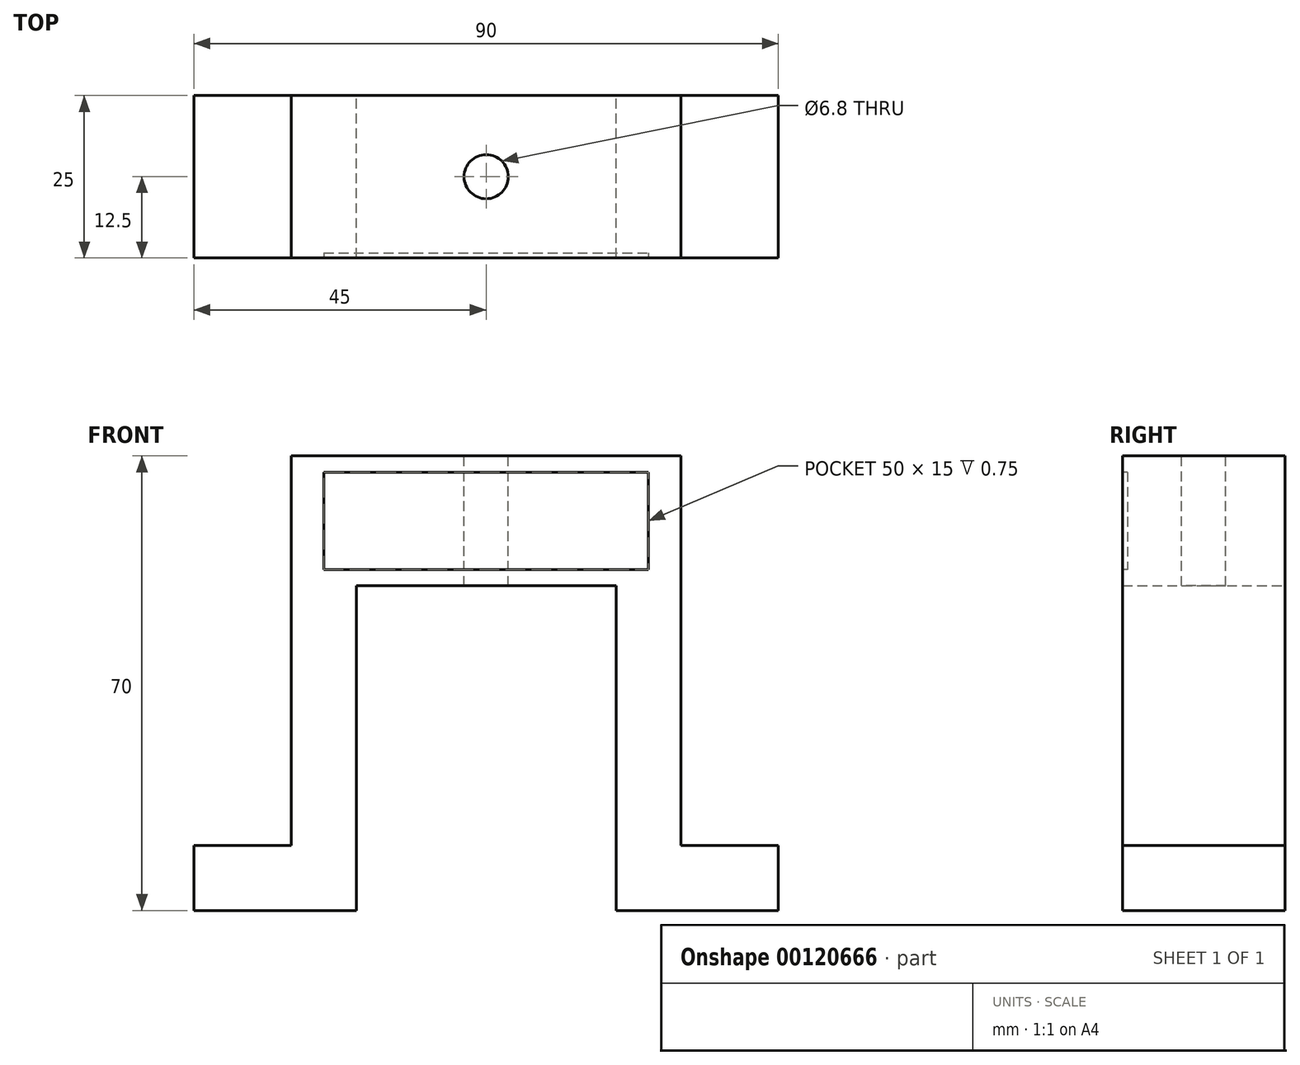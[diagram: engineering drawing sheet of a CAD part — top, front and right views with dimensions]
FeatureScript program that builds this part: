
annotation { "Feature Type Name" : "Feature", "Feature Type Description" : "" }
export const myFeature = defineFeature(function(context is Context, id is Id, definition is map)
    precondition{}
    {
        {
            var Q0;
            Q0=qCreatedBy(makeId("Front.planeOp"),FACE);
            var sketch = newSketch(context, id + "F0", { "sketchPlane" : qUnion([Q0])});
            skLineSegment(sketch, "E0", {"start": v(0, 60) * mm, "end": v(30, 60) * mm});
            skLineSegment(sketch, "E1", {"start": v(30, 60) * mm, "end": v(30, 10) * mm});
            skLineSegment(sketch, "E2", {"start": v(30, 10) * mm, "end": v(45, 10) * mm});
            skLineSegment(sketch, "E3", {"start": v(45, 10) * mm, "end": v(45, 0) * mm});
            skLineSegment(sketch, "E4", {"start": v(45, 0) * mm, "end": v(20, 0) * mm});
            skLineSegment(sketch, "E5", {"start": v(20, 0) * mm, "end": v(20, 50) * mm});
            skLineSegment(sketch, "E6", {"start": v(20, 50) * mm, "end": v(0, 50) * mm});
            skLineSegment(sketch, "E7.MirrorCS", {"start": v(0, 60) * mm, "end": v(-30, 60) * mm});
            skLineSegment(sketch, "E8.MirrorCS", {"start": v(-20, 50) * mm, "end": v(0, 50) * mm});
            skLineSegment(sketch, "E9.MirrorCS", {"start": v(-20, 0) * mm, "end": v(-20, 50) * mm});
            skLineSegment(sketch, "E10.MirrorCS", {"start": v(-30, 60) * mm, "end": v(-30, 10) * mm});
            skLineSegment(sketch, "E11.MirrorCS", {"start": v(-30, 10) * mm, "end": v(-45, 10) * mm});
            skLineSegment(sketch, "E12.MirrorCS", {"start": v(-45, 0) * mm, "end": v(-20, 0) * mm});
            skLineSegment(sketch, "E13.MirrorCS", {"start": v(-45, 10) * mm, "end": v(-45, 0) * mm});
            skSolve(sketch);
        }
        {
            var Q0;
            Q0=makeQuery(id+"F0.imprint","IMPRINT",FACE,{"disambiguationData":[TD([[makeQuery(id+"F0.imprint","IMPRINT",EDGE,{"derivedFrom":sQuery(id+"F0.wireOp",EDGE,"E0")}),-1.0]])]});
            extrude(context, id + "F1", {"entities" : qUnion([Q0]), "depth" : 25 * mm});
        }
        {
            var Q0;
            Q0=makeQuery(id+"F1.opExtrude","SWEPT_FACE",FACE,{"disambiguationData":[OSD([sQuery(id+"F0.wireOp",EDGE,"E0"),sQuery(id+"F0.wireOp",EDGE,"E7.MirrorCS")])]});
            var sketch = newSketch(context, id + "F2", { "sketchPlane" : qUnion([Q0])});
            skPoint(sketch, "E14.0", {"position": v(-30, 0) * mm});
            skPoint(sketch, "E15.0", {"position": v(30, -25) * mm});
            skLineSegment(sketch, "E16", {"start": v(-30, 0) * mm, "end": v(30, -25) * mm, "construction": true});
            skPoint(sketch, "E17", {"position": v(0, -12.5) * mm});
            skSolve(sketch);
        }
        {
            var Q0;
            Q0=sQuery(id+"F2.wireOp",VERTEX,"E17");
            var Q1;
            Q1=makeQuery(id+"F1.opExtrude","SWEPT_BODY",BODY,{"disambiguationData":[OSD([sQuery(id+"F0.wireOp",EDGE,"E0"),sQuery(id+"F0.wireOp",EDGE,"E1"),sQuery(id+"F0.wireOp",EDGE,"E2"),sQuery(id+"F0.wireOp",EDGE,"E3"),sQuery(id+"F0.wireOp",EDGE,"E4"),sQuery(id+"F0.wireOp",EDGE,"E5"),sQuery(id+"F0.wireOp",EDGE,"E6"),sQuery(id+"F0.wireOp",EDGE,"E7.MirrorCS"),sQuery(id+"F0.wireOp",EDGE,"E8.MirrorCS"),sQuery(id+"F0.wireOp",EDGE,"E9.MirrorCS"),sQuery(id+"F0.wireOp",EDGE,"E10.MirrorCS"),sQuery(id+"F0.wireOp",EDGE,"E11.MirrorCS"),sQuery(id+"F0.wireOp",EDGE,"E12.MirrorCS"),sQuery(id+"F0.wireOp",EDGE,"E13.MirrorCS")])]});
            hole(context, id + "F3", {"style" : HoleStyle.SIMPLE, "endStyle" : HoleEndStyle.BLIND, "standardTappedOrClearance" : lookupTablePath({ "standard" : "ISO", "engagement" : "75%", "pitch" : "1.25 mm", "size" : "M8", "type" : "Tapped" }), "standardBlindInLast" : lookupTablePath({ "standard" : "ISO", "engagement" : "75%", "pitch" : "1.25 mm", "size" : "M8", "type" : "Tapped" }), "holeDiameter" : 6.8 * mm, "holeDepth" : 14 * mm, "startFromSketch" : true, "locations" : qUnion([Q0]), "scope" : qUnion([Q1]), "majorDiameter" : 8 * mm});
        }
        {
            var Q0;
            Q0=makeQuery(id+"F1.opExtrude","SWEPT_FACE",FACE,{"disambiguationData":[OSD([sQuery(id+"F0.wireOp",EDGE,"E0"),sQuery(id+"F0.wireOp",EDGE,"E7.MirrorCS")])]});
            extrude(context, id + "F4", {"entities" : qUnion([Q0]), "operationType" : NewBodyOperationType.ADD, "depth" : 10 * mm});
        }
        {
            var Q0;
            {var subQ0=sQuery(id+"F0.wireOp",EDGE,"E7.MirrorCS");var subQ1=sQuery(id+"F0.wireOp",EDGE,"E0");Q0=makeQuery(id+"F4.boolean.opBoolean","MERGE",FACE,{"derivedFrom":[makeQuery(id+"F1.opExtrude","CAP_FACE",FACE,{"disambiguationData":[OSD([subQ1,sQuery(id+"F0.wireOp",EDGE,"E1"),sQuery(id+"F0.wireOp",EDGE,"E2"),sQuery(id+"F0.wireOp",EDGE,"E3"),sQuery(id+"F0.wireOp",EDGE,"E4"),sQuery(id+"F0.wireOp",EDGE,"E5"),sQuery(id+"F0.wireOp",EDGE,"E6"),subQ0,sQuery(id+"F0.wireOp",EDGE,"E8.MirrorCS"),sQuery(id+"F0.wireOp",EDGE,"E9.MirrorCS"),sQuery(id+"F0.wireOp",EDGE,"E10.MirrorCS"),sQuery(id+"F0.wireOp",EDGE,"E11.MirrorCS"),sQuery(id+"F0.wireOp",EDGE,"E12.MirrorCS"),sQuery(id+"F0.wireOp",EDGE,"E13.MirrorCS")])],"isStart":false}),makeQuery(id+"F4.opExtrude","SWEPT_FACE",FACE,{"disambiguationData":[OSD([subQ1,subQ0]),TDD([makeQuery(id+"F1.opExtrude","CAP_EDGE",EDGE,{"disambiguationData":[OSD([subQ1,subQ0])],"isStart":false})])]})]});}
            var sketch = newSketch(context, id + "F5", { "sketchPlane" : qUnion([Q0])});
            skLineSegment(sketch, "E18.0", {"start": v(-20, 50) * mm, "end": v(20, 50) * mm});
            skLineSegment(sketch, "E19.0", {"start": v(-30, 70) * mm, "end": v(30, 70) * mm});
            skLineSegment(sketch, "E20", {"start": v(0, 50) * mm, "end": v(0, 70) * mm, "construction": true});
            skPoint(sketch, "E21", {"position": v(0, 60) * mm});
            skLineSegment(sketch, "E22.bottom", {"start": v(-25, 67.5) * mm, "end": v(25, 67.5) * mm});
            skLineSegment(sketch, "E22.top", {"start": v(-25, 52.5) * mm, "end": v(25, 52.5) * mm});
            skLineSegment(sketch, "E22.left", {"start": v(-25, 67.5) * mm, "end": v(-25, 52.5) * mm});
            skLineSegment(sketch, "E22.right", {"start": v(25, 67.5) * mm, "end": v(25, 52.5) * mm});
            skSolve(sketch);
        }
        {
            var Q0;
            Q0=makeQuery(id+"F5.imprint","IMPRINT",FACE,{"disambiguationData":[TD([[makeQuery(id+"F5.imprint","IMPRINT",EDGE,{"derivedFrom":sQuery(id+"F5.wireOp",EDGE,"E22.bottom")}),-1.0]])]});
            extrude(context, id + "F6", {"entities" : qUnion([Q0]), "operationType" : NewBodyOperationType.REMOVE, "oppositeDirection" : true, "depth" : .75 * mm});
        }
    });
